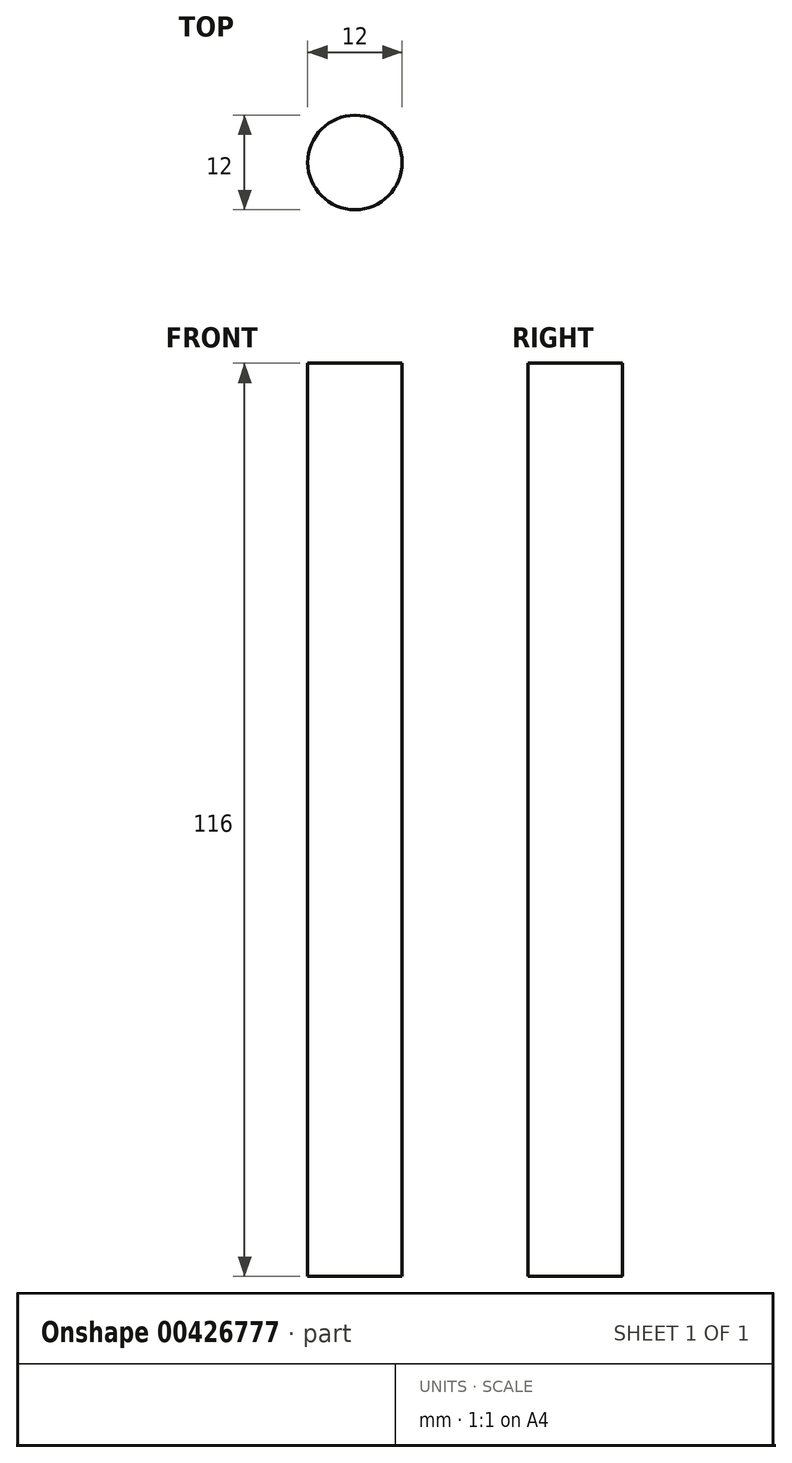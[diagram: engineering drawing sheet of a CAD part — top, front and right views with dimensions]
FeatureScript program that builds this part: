
annotation { "Feature Type Name" : "Feature", "Feature Type Description" : "" }
export const myFeature = defineFeature(function(context is Context, id is Id, definition is map)
    precondition{}
    {
        {
            var Q0;
            Q0=qCreatedBy(makeId("Top.planeOp"),FACE);
            var sketch = newSketch(context, id + "F0", { "sketchPlane" : qUnion([Q0])});
            skCircle(sketch, "E0", {"center": v(0, 0) * mm, "radius": 6 * mm});
            skSolve(sketch);
        }
        {
            var Q0;
            Q0=makeQuery(id+"F0.imprint","IMPRINT",FACE,{"disambiguationData":[TD([[makeQuery(id+"F0.imprint","IMPRINT",EDGE,{"derivedFrom":sQuery(id+"F0.wireOp",EDGE,"E0")}),1.0]])]});
            extrude(context, id + "F1", {"entities" : qUnion([Q0]), "depth" : 116 * mm});
        }
    });
